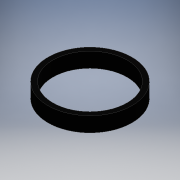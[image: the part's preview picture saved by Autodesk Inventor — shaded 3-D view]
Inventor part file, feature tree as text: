
AUTODESK INVENTOR PART (.ipt)
format: ipt  version: 2016 (Build 200138000, 138)  size: 96,256 bytes
history: native  units: mm
features: other x1, extrude x1, sketch x1
ambient origin geometry x8: Origin, YZ Plane, XZ Plane, XY Plane, X Axis, Y Axis, Z Axis, Center Point
bodies: Body1 (feature_tree)
feature tree (3):
  other  "ソリッド1"
  extrude  "押し出し1"  Depth=15.0mm
  sketch  "スケッチ1"
